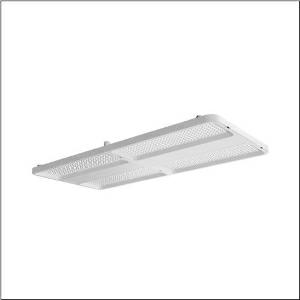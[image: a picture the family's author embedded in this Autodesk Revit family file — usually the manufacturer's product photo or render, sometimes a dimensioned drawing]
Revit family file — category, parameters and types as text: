
# Revit family: highbay_11_maxi_51hn11db4lda02
name_source: partatom
category: Lighting Fixtures
units: mm (PartAtom-declared; Revit-internal decimal feet)

## family parameters
Cut with Voids When Loaded = No
Host = Face
Light Source = No
Part Type = Normal
Room Calculation Point = No
Round Connector Dimension = Use Diameter
Shared = No

## types (1)
- --- (1 x LED, 26000 lm, 125.9 W, 4000K)
    Apparent Load = 126 VA
    CIE Flux Codes = 85 97 100 100 100
    Color Rendering = 80
    Color Temperature = 4000K
    Default Elevation = 1800 mm
    Description = high bay luminaire Highbay 11 maxi; direct symmetric narrow distribution, light control with lens of PMMA; UGR ≤ 19 (X = 4H | Y = 8H | S = 0.25H | reflection values 70/50/20); luminous flux: 26.000lm; light colour: 840, colour temperature: 4000K, MacAdam ≤ 2 SDCM (initial), colour rendering: CRI > 80; luminous efficacy: 206,5lm/W; rated service life: 100.000h (L95/B50) at AT= 25°C; control: Bluetooth® Mesh; for wireless networking: Node luminaire for setting up a local control solution without a higher-level application controller, intelligence completely in the luminaire; no control line such as DALI between the Node multi-sensor luminaires and Nodes is required, wireless integration of other Node luminaires and Node multi-sensor luminaires into the network is possible; number of Node luminaires in the project can be expanded as required, network sizes > 300 Nodes can be realized; can also be connected to lighting or building automation via various gateways upon request; integrated DALI2 ECG provides luminaire data (according to IEC62386, Part 251), energy data (Part 252), and monitoring and analytics data (Part 253) to higher-level systems for further processing; luminaire connection: terminal, 5-pole, max. 2.5mm² (cable entry for one cable, Ø 8.5..16mm); mains connection: 230..240V, AC 50/60Hz; connected load: 125,9W; protection rating (complete): IP66; insulation class (complete): insulation class I (protective earthing); protection symbol: D; impact resistance: IK08; certification: CE, ENEC, VDE, UKCA; internal wiring halogen-free; luminaire corresponds to IFS (International Featured Standards) requirements for safety and quality in the food industry; LABS conformity tested according to VDMA 24364:2018-05; housing frame of high-performance plastic PA6, matt traffic white (RAL 9016); cover of PMMA; dimension (LxWxH): 946 x 442 x 72mm; permissible operating ambient temperature: -20..+45°C (reducing of maximum allowable ambient temperature of 5°C with ceiling mounting); packaging unit: 1 piece; (delivery without accessories; please order mounting accessories separately)
    Height = 72 mm  [stored 0.23622 ft]
    Lamp = 1 x LED
    Lamp Light Flux = 26000 lm
    Lamp Power = 125.9 W
    Lamp count = 1
    Length = 946 mm
    Luminous efficacy = 207 lm/W
    Manufacturer = Siteco
    ModVariant = No
    Model = 51HN11DB4LDA02
    Mounting Place = Ceiling
    Mounting Type = Pendant
    Number of Poles = 1
    OnlyDefault = Yes
    Power Factor = 1
    Product Name = Highbay 11 maxi
    Product group = high bay luminaire
    ProductGroupID = 901
    Protection Class = Protection class I
    Protection Degree = IP 66
    RLX_Detail_Level = 1
    RLX_Emergency_Light_Flux = 0 lm
    RLX_Emergency_Type = 0
    RLX_Emergency_Type_DB = No
    RlxData = <blob elided: 127893 chars, md5=6e39bca6>
    Socket = socket
    Standby Power = 0 W
    System Light Flux = 26000 lm
    System Power = 126 W
    Type Comments = factory setting: luminous flux: 100 % | dim-lin: 254 | 584 mA
    Type Image = l_1363244.jpg
    URL = http://relux.com
    VarID = @adj_022629
    Voltage = 0 V
    Weight = 0.00 kg
    Width = 442 mm

note: [stored X ft] marks values corroborated as IEEE doubles in the binary element streams (Revit-internal decimal feet)

## geometry (parser evidence)
native form markers: Blend x4, Sweep x10
no freeform markers — native parametric forms only
